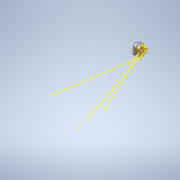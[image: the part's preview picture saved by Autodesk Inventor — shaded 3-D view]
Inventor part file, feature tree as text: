
AUTODESK INVENTOR PART (.ipt)
format: ipt  version: 2020 (Build 240168000, 168)  size: 315,392 bytes
history: native  units: mm
features: sketch x7, other x4, projected_geometry x3, extrude x2
ambient origin geometry x8: Origin, YZ Plane, XZ Plane, XY Plane, X Axis, Y Axis, Z Axis, Center Point
bodies: Solid1 (feature_tree)
feature tree (16):
  other  "preadator nano fixed mount template.iam"
  other  "Kauri modular camera mount HDzero micro v1 mirror.ipt:1"
  other  "Kauri modular camera mount HDzero micro v1.ipt:1"
  other  "camera housing V1.ipt:1"
  extrude  "Extrusion1"  Depth=10.0mm TaperAngle=0.0deg
  extrude  "Extrusion2"  [1 undecoded]
  sketch  "Sketch1"  dims[d0=10.0mm d1=10.0mm d2=0.0mm]
  sketch  "Sketch1_1"  dims[d3=10.0mm d4=0.0mm]
  sketch  "Sketch6"
  sketch  "Sketch10"
  sketch  "Sketch11"
  sketch  "Sketch7"
  projected_geometry  "Projected Loop1"
  sketch  "Sketch8"
  projected_geometry  "Projected Loop2"
  projected_geometry  "Projected Loop3"
note: 1 required parameter value undecoded (feature->parameter linkage not recoverable at this tier; creation-order binding heuristic only, values carry confidence <= 0.55)
